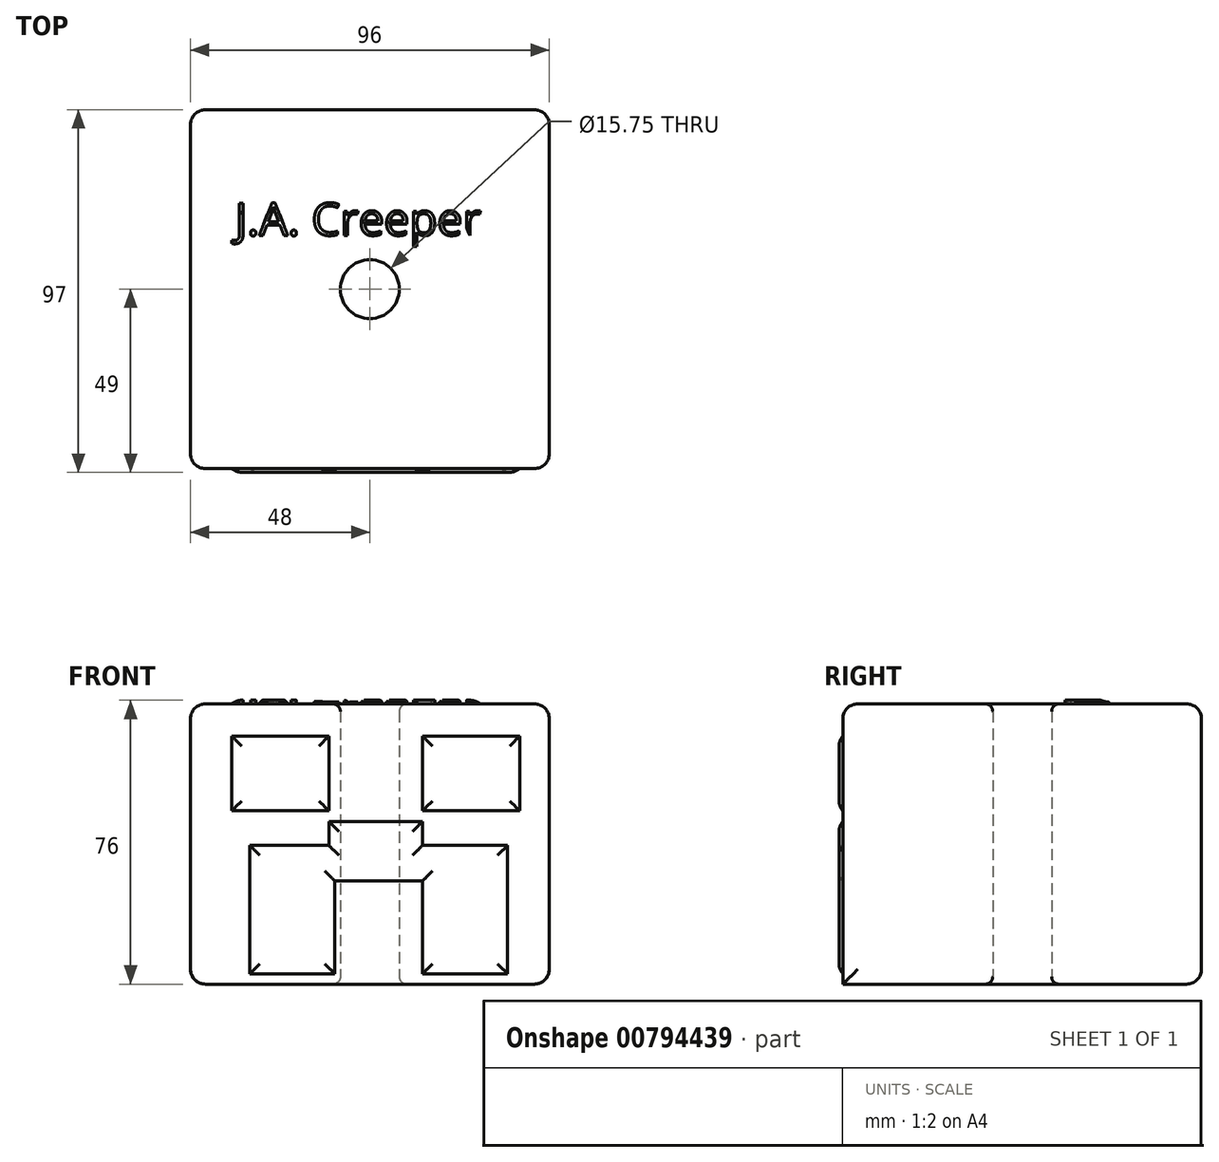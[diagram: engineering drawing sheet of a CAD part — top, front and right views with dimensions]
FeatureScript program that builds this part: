
annotation { "Feature Type Name" : "Feature", "Feature Type Description" : "" }
export const myFeature = defineFeature(function(context is Context, id is Id, definition is map)
    precondition{}
    {
        {
            var Q0;
            Q0=qCreatedBy(makeId("Top.planeOp"),FACE);
            var sketch = newSketch(context, id + "F0", { "sketchPlane" : qUnion([Q0])});
            skLineSegment(sketch, "E0.bottom", {"start": v(-48, 48) * mm, "end": v(48, 48) * mm});
            skLineSegment(sketch, "E0.top", {"start": v(-48, -48) * mm, "end": v(48, -48) * mm});
            skLineSegment(sketch, "E0.left", {"start": v(-48, 48) * mm, "end": v(-48, -48) * mm});
            skLineSegment(sketch, "E0.right", {"start": v(48, 48) * mm, "end": v(48, -48) * mm});
            skPoint(sketch, "E0.middle", {"position": v(0, 0) * mm});
            skCircle(sketch, "E1", {"center": v(0, 0) * mm, "radius": 7.88 * mm});
            skSolve(sketch);
        }
        {
            var Q0;
            Q0 = qSketchRegion(id + "F0", true);
            extrude(context, id + "F1", {"entities" : qUnion([Q0]), "depth" : 75 * mm, "offsetDistance" : 25 * mm});
        }
        {
            var Q0;
            Q0=makeQuery(id+"F1.opExtrude","SWEPT_FACE",FACE,{"disambiguationData":[OSD([sQuery(id+"F0.wireOp",EDGE,"E0.top")])]});
            var sketch = newSketch(context, id + "F2", { "sketchPlane" : qUnion([Q0])});
            skLineSegment(sketch, "E2.bottom", {"start": v(-36.97, 66.38) * mm, "end": v(-10.97, 66.38) * mm});
            skLineSegment(sketch, "E2.top", {"start": v(-36.97, 46.38) * mm, "end": v(-10.97, 46.38) * mm});
            skLineSegment(sketch, "E2.left", {"start": v(-36.97, 66.38) * mm, "end": v(-36.97, 46.38) * mm});
            skLineSegment(sketch, "E2.right", {"start": v(-10.97, 66.38) * mm, "end": v(-10.97, 46.38) * mm});
            skPoint(sketch, "E2.middle", {"position": v(-23.97, 56.38) * mm});
            skLineSegment(sketch, "E3.bottom", {"start": v(14.09, 66.38) * mm, "end": v(40.09, 66.38) * mm});
            skLineSegment(sketch, "E3.top", {"start": v(14.09, 46.38) * mm, "end": v(40.09, 46.38) * mm});
            skLineSegment(sketch, "E3.left", {"start": v(14.09, 66.38) * mm, "end": v(14.09, 46.38) * mm});
            skLineSegment(sketch, "E3.right", {"start": v(40.09, 66.38) * mm, "end": v(40.09, 46.38) * mm});
            skPoint(sketch, "E3.middle", {"position": v(27.09, 56.38) * mm});
            skLineSegment(sketch, "E4", {"start": v(-32.1, 2.77) * mm, "end": v(-9.38, 2.77) * mm});
            skLineSegment(sketch, "E5", {"start": v(-9.38, 2.77) * mm, "end": v(-9.38, 27.62) * mm});
            skLineSegment(sketch, "E6", {"start": v(-9.38, 27.62) * mm, "end": v(14.09, 27.62) * mm});
            skLineSegment(sketch, "E7", {"start": v(14.09, 27.62) * mm, "end": v(14.09, 2.77) * mm});
            skLineSegment(sketch, "E8", {"start": v(14.09, 2.77) * mm, "end": v(36.86, 2.77) * mm});
            skLineSegment(sketch, "E9", {"start": v(36.86, 2.77) * mm, "end": v(36.86, 37.13) * mm});
            skLineSegment(sketch, "E10", {"start": v(36.86, 37.13) * mm, "end": v(14.09, 37.13) * mm});
            skLineSegment(sketch, "E11", {"start": v(-10.97, 37.13) * mm, "end": v(-32.1, 37.13) * mm});
            skLineSegment(sketch, "E12", {"start": v(-32.1, 37.13) * mm, "end": v(-32.1, 2.77) * mm});
            skLineSegment(sketch, "E13", {"start": v(14.09, 37.13) * mm, "end": v(14.09, 43.52) * mm});
            skLineSegment(sketch, "E14", {"start": v(14.09, 43.52) * mm, "end": v(-10.97, 43.52) * mm});
            skLineSegment(sketch, "E15", {"start": v(-10.97, 37.13) * mm, "end": v(-10.97, 43.52) * mm});
            skSolve(sketch);
        }
        {
            var Q0;
            Q0 = qSketchRegion(id + "F2", true);
            extrude(context, id + "F3", {"entities" : qUnion([Q0]), "operationType" : NewBodyOperationType.ADD, "depth" : 1 * mm, "offsetDistance" : 25 * mm});
        }
        {
            var Q0;
            Q0=makeQuery(id+"F1.opExtrude","CAP_FACE",FACE,{"disambiguationData":[OSD([sQuery(id+"F0.wireOp",EDGE,"E0.bottom"),sQuery(id+"F0.wireOp",EDGE,"E0.top"),sQuery(id+"F0.wireOp",EDGE,"E0.left"),sQuery(id+"F0.wireOp",EDGE,"E0.right")])],"isStart":false});
            var sketch = newSketch(context, id + "F4", { "sketchPlane" : qUnion([Q0])});
            skText(sketch, "E16", { "text": "J.A. Creeper", "fontName": "OpenSans-Regular.ttf"});
            const initialGuessF4  = {"E16": [-0.03607, 0.0144, 1, 0, 0.00872]};
            skSetInitialGuess(sketch, initialGuessF4);
            skSolve(sketch);
        }
        {
            var Q0;
            Q0 = qSketchRegion(id + "F4", true);
            extrude(context, id + "F5", {"entities" : qUnion([Q0]), "operationType" : NewBodyOperationType.ADD, "depth" : 1 * mm, "offsetDistance" : 25 * mm});
        }
        {
            var Q0;
            Q0=makeQuery(id+"F3.opExtrude","CAP_EDGE",EDGE,{"disambiguationData":[OSD([sQuery(id+"F2.wireOp",EDGE,"E2.bottom")])],"isStart":false});
            var Q1;
            Q1=makeQuery(id+"F3.opExtrude","CAP_EDGE",EDGE,{"disambiguationData":[OSD([sQuery(id+"F2.wireOp",EDGE,"E2.left")])],"isStart":false});
            var Q2;
            Q2=makeQuery(id+"F3.opExtrude","CAP_EDGE",EDGE,{"disambiguationData":[OSD([sQuery(id+"F2.wireOp",EDGE,"E2.top")])],"isStart":false});
            var Q3;
            Q3=makeQuery(id+"F3.opExtrude","CAP_EDGE",EDGE,{"disambiguationData":[OSD([sQuery(id+"F2.wireOp",EDGE,"E2.right")])],"isStart":false});
            var Q4;
            Q4=makeQuery(id+"F3.opExtrude","CAP_FACE",FACE,{"disambiguationData":[OSD([sQuery(id+"F2.wireOp",EDGE,"E3.bottom"),sQuery(id+"F2.wireOp",EDGE,"E3.top"),sQuery(id+"F2.wireOp",EDGE,"E3.left"),sQuery(id+"F2.wireOp",EDGE,"E3.right")])],"isStart":false});
            var Q5;
            Q5=makeQuery(id+"F3.opExtrude","CAP_FACE",FACE,{"disambiguationData":[OSD([sQuery(id+"F2.wireOp",EDGE,"E4"),sQuery(id+"F2.wireOp",EDGE,"E5"),sQuery(id+"F2.wireOp",EDGE,"E6"),sQuery(id+"F2.wireOp",EDGE,"E7"),sQuery(id+"F2.wireOp",EDGE,"E8"),sQuery(id+"F2.wireOp",EDGE,"E9"),sQuery(id+"F2.wireOp",EDGE,"E10"),sQuery(id+"F2.wireOp",EDGE,"E11"),sQuery(id+"F2.wireOp",EDGE,"E12"),sQuery(id+"F2.wireOp",EDGE,"E13"),sQuery(id+"F2.wireOp",EDGE,"E14"),sQuery(id+"F2.wireOp",EDGE,"E15")])],"isStart":false});
            var Q6;
            Q6=makeQuery(id+"F1.opExtrude","CAP_EDGE",EDGE,{"disambiguationData":[OSD([sQuery(id+"F0.wireOp",EDGE,"E0.top")])],"isStart":false});
            var Q7;
            Q7=makeQuery(id+"F1.opExtrude","CAP_EDGE",EDGE,{"disambiguationData":[OSD([sQuery(id+"F0.wireOp",EDGE,"E0.right")])],"isStart":false});
            var Q8;
            Q8=makeQuery(id+"F1.opExtrude","CAP_EDGE",EDGE,{"disambiguationData":[OSD([sQuery(id+"F0.wireOp",EDGE,"E0.left")])],"isStart":false});
            var Q9;
            Q9=makeQuery(id+"F1.opExtrude","CAP_EDGE",EDGE,{"disambiguationData":[OSD([sQuery(id+"F0.wireOp",EDGE,"E0.bottom")])],"isStart":false});
            var Q10;
            Q10=makeQuery(id+"F1.opExtrude","SWEPT_EDGE",EDGE,{"disambiguationData":[OSD([sQuery(id+"F0.wireOp",EDGE,"E0.bottom"),sQuery(id+"F0.wireOp",EDGE,"E0.left")])]});
            var Q11;
            Q11=makeQuery(id+"F1.opExtrude","SWEPT_EDGE",EDGE,{"disambiguationData":[OSD([sQuery(id+"F0.wireOp",EDGE,"E0.bottom"),sQuery(id+"F0.wireOp",EDGE,"E0.right")])]});
            var Q12;
            Q12=makeQuery(id+"F1.opExtrude","CAP_EDGE",EDGE,{"disambiguationData":[OSD([sQuery(id+"F0.wireOp",EDGE,"E0.bottom")])],"isStart":true});
            var Q13;
            Q13=makeQuery(id+"F1.opExtrude","CAP_EDGE",EDGE,{"disambiguationData":[OSD([sQuery(id+"F0.wireOp",EDGE,"E0.left")])],"isStart":true});
            var Q14;
            Q14=makeQuery(id+"F1.opExtrude","CAP_EDGE",EDGE,{"disambiguationData":[OSD([sQuery(id+"F0.wireOp",EDGE,"E0.right")])],"isStart":true});
            var Q15;
            Q15=makeQuery(id+"F1.opExtrude","SWEPT_EDGE",EDGE,{"disambiguationData":[OSD([sQuery(id+"F0.wireOp",EDGE,"E0.top"),sQuery(id+"F0.wireOp",EDGE,"E0.left")])]});
            var Q16;
            Q16=makeQuery(id+"F1.opExtrude","SWEPT_EDGE",EDGE,{"disambiguationData":[OSD([sQuery(id+"F0.wireOp",EDGE,"E0.top"),sQuery(id+"F0.wireOp",EDGE,"E0.right")])]});
            fillet(context, id + "F6", {"entities" : qUnion([Q0, Q1, Q2, Q3, Q4, Q5, Q6, Q7, Q8, Q9, Q10, Q11, Q12, Q13, Q14, Q15, Q16]), "radius" : 4 * mm, "tangentPropagation" : true, "allowEdgeOverflow" : false});
        }
        {
            var Q0;
            Q0=makeQuery(id+"F5.opExtrude","CAP_EDGE",EDGE,{"disambiguationData":[OSD([sQuery(id+"F4.wireOp",EDGE,"E16.sketch_text.stroke-25")])],"isStart":false});
            var Q1;
            Q1=makeQuery(id+"F5.opExtrude","CAP_EDGE",EDGE,{"disambiguationData":[OSD([sQuery(id+"F4.wireOp",EDGE,"E16.sketch_text.stroke-23")])],"isStart":false});
            var Q2;
            Q2=makeQuery(id+"F5.opExtrude","CAP_EDGE",EDGE,{"disambiguationData":[OSD([sQuery(id+"F4.wireOp",EDGE,"E16.sketch_text.stroke-6")])],"isStart":false});
            var Q3;
            Q3=makeQuery(id+"F5.opExtrude","CAP_EDGE",EDGE,{"disambiguationData":[OSD([sQuery(id+"F4.wireOp",EDGE,"E16.sketch_text.stroke-1")])],"isStart":false});
            var Q4;
            Q4=makeQuery(id+"F5.opExtrude","CAP_EDGE",EDGE,{"disambiguationData":[OSD([sQuery(id+"F4.wireOp",EDGE,"E16.sketch_text.stroke-39")])],"isStart":false});
            var Q5;
            Q5=makeQuery(id+"F5.opExtrude","CAP_EDGE",EDGE,{"disambiguationData":[OSD([sQuery(id+"F4.wireOp",EDGE,"E16.sketch_text.stroke-57")])],"isStart":false});
            var Q6;
            Q6=makeQuery(id+"F5.opExtrude","CAP_EDGE",EDGE,{"disambiguationData":[OSD([sQuery(id+"F4.wireOp",EDGE,"E16.sketch_text.stroke-74")])],"isStart":false});
            var Q7;
            Q7=makeQuery(id+"F5.opExtrude","CAP_EDGE",EDGE,{"disambiguationData":[OSD([sQuery(id+"F4.wireOp",EDGE,"E16.sketch_text.stroke-93")])],"isStart":false});
            var Q8;
            Q8=makeQuery(id+"F5.opExtrude","CAP_EDGE",EDGE,{"disambiguationData":[OSD([sQuery(id+"F4.wireOp",EDGE,"E16.sketch_text.stroke-76")])],"isStart":false});
            var Q9;
            Q9=makeQuery(id+"F5.opExtrude","CAP_EDGE",EDGE,{"disambiguationData":[OSD([sQuery(id+"F4.wireOp",EDGE,"E16.sketch_text.stroke-95")])],"isStart":false});
            var Q10;
            Q10=makeQuery(id+"F5.opExtrude","CAP_EDGE",EDGE,{"disambiguationData":[OSD([sQuery(id+"F4.wireOp",EDGE,"E16.sketch_text.stroke-137")])],"isStart":false});
            var Q11;
            Q11=makeQuery(id+"F5.opExtrude","CAP_EDGE",EDGE,{"disambiguationData":[OSD([sQuery(id+"F4.wireOp",EDGE,"E16.sketch_text.stroke-139")])],"isStart":false});
            var Q12;
            Q12=makeQuery(id+"F5.opExtrude","CAP_EDGE",EDGE,{"disambiguationData":[OSD([sQuery(id+"F4.wireOp",EDGE,"E16.sketch_text.stroke-150")])],"isStart":false});
            var Q13;
            Q13=makeQuery(id+"F5.opExtrude","SWEPT_EDGE",EDGE,{"disambiguationData":[OSD([sQuery(id+"F4.wireOp",EDGE,"E16.sketch_text.stroke-155"),sQuery(id+"F4.wireOp",EDGE,"E16.sketch_text.stroke-156")])]});
            fillet(context, id + "F7", {"entities" : qUnion([Q0, Q1, Q2, Q3, Q4, Q5, Q6, Q7, Q8, Q9, Q10, Q11, Q12, Q13]), "radius" : 5 * mm, "tangentPropagation" : true, "allowEdgeOverflow" : false});
        }
        {
            var Q0;
            Q0=makeQuery(id+"F1.opExtrude","CAP_EDGE",EDGE,{"disambiguationData":[OSD([sQuery(id+"F0.wireOp",EDGE,"E1")])],"isStart":false});
            var Q1;
            Q1=makeQuery(id+"F1.opExtrude","CAP_EDGE",EDGE,{"disambiguationData":[OSD([sQuery(id+"F0.wireOp",EDGE,"E1")])],"isStart":true});
            fillet(context, id + "F8", {"entities" : qUnion([Q0, Q1]), "radius" : 2 * mm, "tangentPropagation" : true, "allowEdgeOverflow" : false});
        }
    });
